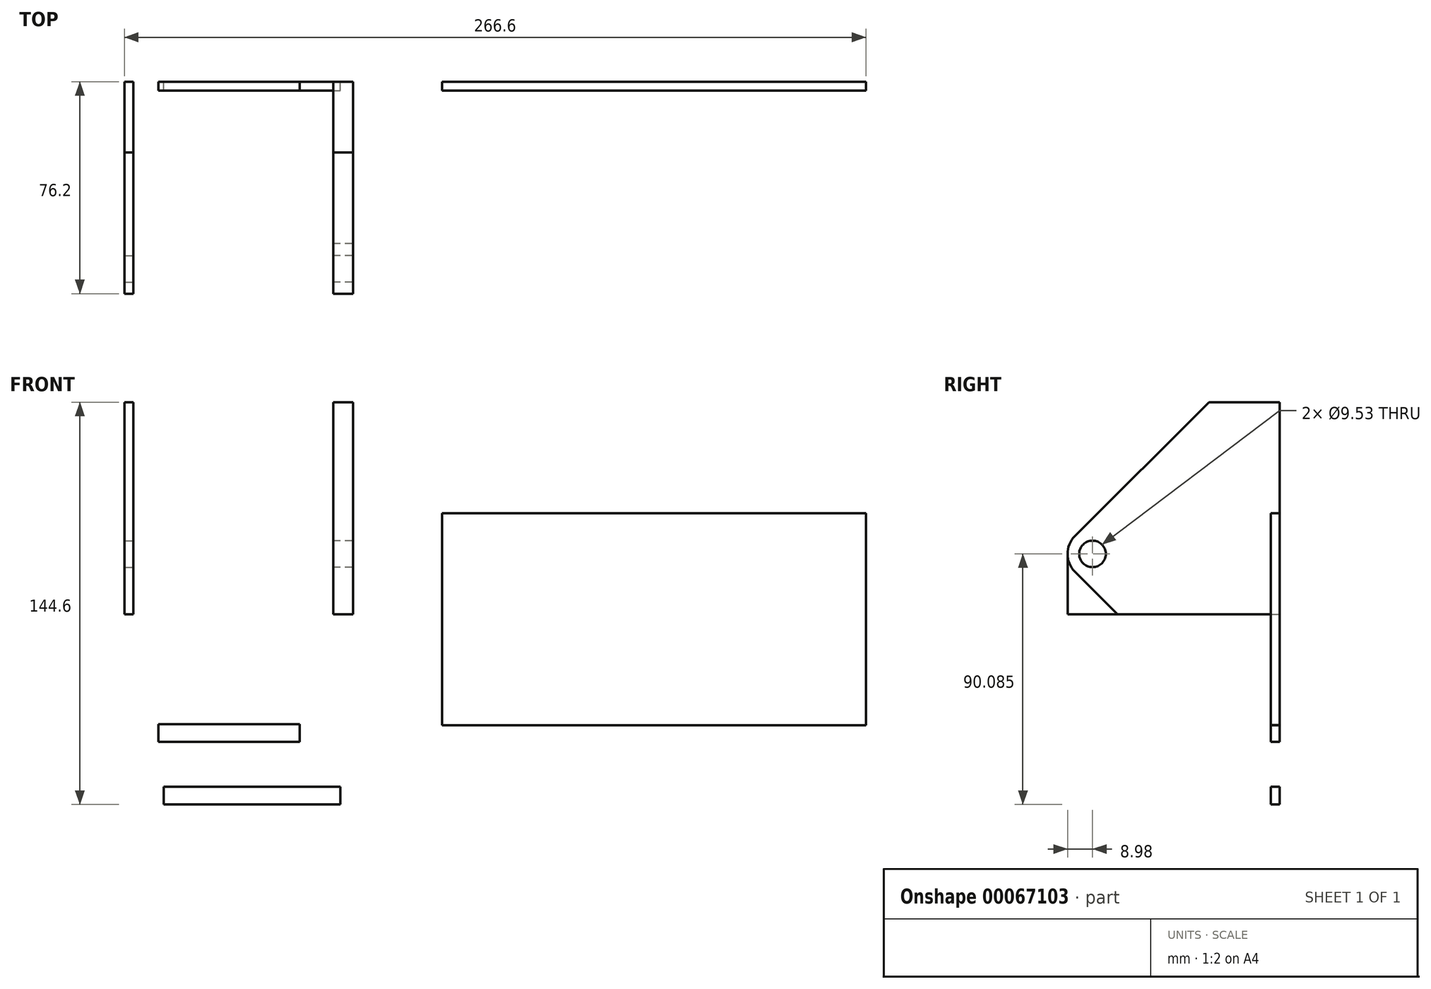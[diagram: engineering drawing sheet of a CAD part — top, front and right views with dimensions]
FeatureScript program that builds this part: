
annotation { "Feature Type Name" : "Feature", "Feature Type Description" : "" }
export const myFeature = defineFeature(function(context is Context, id is Id, definition is map)
    precondition{}
    {
        {
            var Q0;
            Q0=qCreatedBy(makeId("Front.planeOp"),FACE);
            var sketch = newSketch(context, id + "F0", { "sketchPlane" : qUnion([Q0])});
            skLineSegment(sketch, "E0.bottom", {"start": v(-75.12, 82.71) * mm, "end": v(-71.94, 82.71) * mm});
            skLineSegment(sketch, "E0.top", {"start": v(-75.12, 6.51) * mm, "end": v(-71.94, 6.51) * mm});
            skLineSegment(sketch, "E0.left", {"start": v(-75.12, 82.71) * mm, "end": v(-75.12, 6.51) * mm});
            skLineSegment(sketch, "E0.right", {"start": v(-71.94, 82.71) * mm, "end": v(-71.94, 6.51) * mm});
            skSolve(sketch);
        }
        {
            var Q0;
            Q0=makeQuery(id+"F0.imprint","IMPRINT",FACE,{"disambiguationData":[TD([[makeQuery(id+"F0.imprint","IMPRINT",EDGE,{"derivedFrom":sQuery(id+"F0.wireOp",EDGE,"E0.bottom")}),-1.0]])]});
            extrude(context, id + "F1", {"entities" : qUnion([Q0]), "depth" : 76.2 * mm});
        }
        {
            var Q0;
            Q0=makeQuery(id+"F1.opExtrude","SWEPT_FACE",FACE,{"disambiguationData":[OSD([sQuery(id+"F0.wireOp",EDGE,"E0.right")])]});
            var sketch = newSketch(context, id + "F2", { "sketchPlane" : qUnion([Q0])});
            skLineSegment(sketch, "E1.0", {"start": v(-76.2, 82.71) * mm, "end": v(0, 82.71) * mm});
            skLineSegment(sketch, "E1.1", {"start": v(-76.2, 82.71) * mm, "end": v(-76.2, 6.51) * mm});
            skLineSegment(sketch, "E1.2", {"start": v(-76.2, 6.51) * mm, "end": v(0, 6.51) * mm});
            skLineSegment(sketch, "E1.3", {"start": v(0, 82.71) * mm, "end": v(0, 6.51) * mm});
            skLineSegment(sketch, "E2", {"start": v(0, 6.51) * mm, "end": v(-76.2, 6.51) * mm});
            skLineSegment(sketch, "E3", {"start": v(-76.2, 31.91) * mm, "end": v(-25.4, 82.71) * mm});
            skLineSegment(sketch, "E4", {"start": v(-25.4, 82.71) * mm, "end": v(0, 82.71) * mm});
            skCircle(sketch, "E5", {"center": v(-67.22, 28.2) * mm, "radius": 8.98 * mm});
            skCircle(sketch, "E6", {"center": v(-67.22, 28.2) * mm, "radius": 4.76 * mm});
            skSolve(sketch);
        }
        {
            var Q0;
            Q0=makeQuery(id+"F2.imprint","IMPRINT",FACE,{"disambiguationData":[TD([[makeQuery(id+"F2.imprint","IMPRINT",EDGE,{"derivedFrom":sQuery(id+"F2.wireOp",EDGE,"E6")}),1.0]])]});
            var Q1;
            {var subQ0=sQuery(id+"F2.wireOp",EDGE,"E1.0");Q1=makeQuery(id+"F2.imprint","IMPRINT",FACE,{"disambiguationData":[TD([[makeQuery(id+"F2.imprint","IMPRINT",EDGE,{"derivedFrom":subQ0}),-1.0]])]});}
            var Q2;
            {var subQ0=sQuery(id+"F2.wireOp",EDGE,"E3");var subQ1=sQuery(id+"F2.wireOp",EDGE,"E1.1");var subQ2=makeQuery(id+"F2.imprint","INTERSECT",VERTEX,{"derivedFrom":[subQ1,subQ0]});Q2=makeQuery(id+"F2.imprint","IMPRINT",FACE,{"disambiguationData":[TD([[makeQuery(id+"F2.imprint","IMPRINT",EDGE,{"disambiguationData":[TD([[subQ2,-1.0]])],"derivedFrom":subQ1}),1.0]])]});}
            extrude(context, id + "F3", {"entities" : qUnion([Q0, Q1, Q2]), "operationType" : NewBodyOperationType.REMOVE, "endBound" : BoundingType.THROUGH_ALL, "oppositeDirection" : true, "depth" : 25.4 * mm});
        }
        {
            var Q0;
            Q0=qCreatedBy(makeId("Right.planeOp"),FACE);
            var sketch = newSketch(context, id + "F4", { "sketchPlane" : qUnion([Q0])});
            skLineSegment(sketch, "E7.0", {"start": v(-73.57, 34.55) * mm, "end": v(-25.4, 82.71) * mm});
            skLineSegment(sketch, "E7.1", {"start": v(-25.4, 82.71) * mm, "end": v(0, 82.71) * mm});
            skLineSegment(sketch, "E7.2", {"start": v(0, 82.71) * mm, "end": v(0, 6.51) * mm});
            skLineSegment(sketch, "E7.3", {"start": v(-76.2, 6.51) * mm, "end": v(0, 6.51) * mm});
            skLineSegment(sketch, "E7.4", {"start": v(-76.2, 28.2) * mm, "end": v(-76.2, 6.51) * mm});
            skArc(sketch, "E7.5", {"start": v(-73.57, 34.55) * mm, "mid": v(-75.52, 31.63) * mm, "end": v(-76.2, 28.2) * mm});
            skCircle(sketch, "E8.0", {"center": v(-67.22, 28.2) * mm, "radius": 8.98 * mm});
            skCircle(sketch, "E8.1", {"center": v(-67.22, 28.2) * mm, "radius": 4.76 * mm});
            skLineSegment(sketch, "E9", {"start": v(-73.57, 21.85) * mm, "end": v(-58.24, 6.51) * mm});
            skSolve(sketch);
        }
        {
            var Q0;
            {var subQ3=sQuery(id+"F4.wireOp",EDGE,"E7.0");Q0=makeQuery(id+"F4.imprint","IMPRINT",FACE,{"disambiguationData":[TD([[makeQuery(id+"F4.imprint","IMPRINT",EDGE,{"derivedFrom":subQ3}),-1.0]])]});}
            var Q1;
            Q1=makeQuery(id+"F4.imprint","IMPRINT",FACE,{"disambiguationData":[TD([[makeQuery(id+"F4.imprint","IMPRINT",EDGE,{"derivedFrom":sQuery(id+"F4.wireOp",EDGE,"E8.1")}),-1.0]])]});
            extrude(context, id + "F5", {"entities" : qUnion([Q0, Q1]), "depth" : 7.14 * mm});
        }
        {
            var Q0;
            Q0=qCreatedBy(makeId("Front.planeOp"),FACE);
            var sketch = newSketch(context, id + "F6", { "sketchPlane" : qUnion([Q0])});
            skLineSegment(sketch, "E10.bottom", {"start": v(-62.88, -32.96) * mm, "end": v(-12.08, -32.96) * mm});
            skLineSegment(sketch, "E10.top", {"start": v(-62.88, -39.3) * mm, "end": v(-12.08, -39.3) * mm});
            skLineSegment(sketch, "E10.left", {"start": v(-62.88, -32.96) * mm, "end": v(-62.88, -39.3) * mm});
            skLineSegment(sketch, "E10.right", {"start": v(-12.08, -32.96) * mm, "end": v(-12.08, -39.3) * mm});
            skLineSegment(sketch, "E11.bottom", {"start": v(-61, -55.54) * mm, "end": v(2.5, -55.54) * mm});
            skLineSegment(sketch, "E11.top", {"start": v(-61, -61.89) * mm, "end": v(2.5, -61.89) * mm});
            skLineSegment(sketch, "E11.left", {"start": v(-61, -55.54) * mm, "end": v(-61, -61.89) * mm});
            skLineSegment(sketch, "E11.right", {"start": v(2.5, -55.54) * mm, "end": v(2.5, -61.89) * mm});
            skSolve(sketch);
        }
        {
            var Q0;
            Q0=makeQuery(id+"F6.imprint","IMPRINT",FACE,{"disambiguationData":[TD([[makeQuery(id+"F6.imprint","IMPRINT",EDGE,{"derivedFrom":sQuery(id+"F6.wireOp",EDGE,"E10.bottom")}),-1.0]])]});
            var Q1;
            Q1=makeQuery(id+"F6.imprint","IMPRINT",FACE,{"disambiguationData":[TD([[makeQuery(id+"F6.imprint","IMPRINT",EDGE,{"derivedFrom":sQuery(id+"F6.wireOp",EDGE,"E11.bottom")}),-1.0]])]});
            extrude(context, id + "F7", {"entities" : qUnion([Q0, Q1]), "depth" : 3.17 * mm});
        }
        {
            var Q0;
            Q0=qCreatedBy(makeId("Front.planeOp"),FACE);
            var sketch = newSketch(context, id + "F8", { "sketchPlane" : qUnion([Q0])});
            skLineSegment(sketch, "E12.bottom", {"start": v(191.48, 42.8) * mm, "end": v(39.08, 42.8) * mm});
            skLineSegment(sketch, "E12.top", {"start": v(191.48, -33.4) * mm, "end": v(39.08, -33.4) * mm});
            skLineSegment(sketch, "E12.left", {"start": v(191.48, 42.8) * mm, "end": v(191.48, -33.4) * mm});
            skLineSegment(sketch, "E12.right", {"start": v(39.08, 42.8) * mm, "end": v(39.08, -33.4) * mm});
            skSolve(sketch);
        }
        {
            var Q0;
            Q0=makeQuery(id+"F8.imprint","IMPRINT",FACE,{"disambiguationData":[TD([[makeQuery(id+"F8.imprint","IMPRINT",EDGE,{"derivedFrom":sQuery(id+"F8.wireOp",EDGE,"E12.bottom")}),1.0]])]});
            extrude(context, id + "F9", {"entities" : qUnion([Q0]), "depth" : 3.17 * mm});
        }
    });
